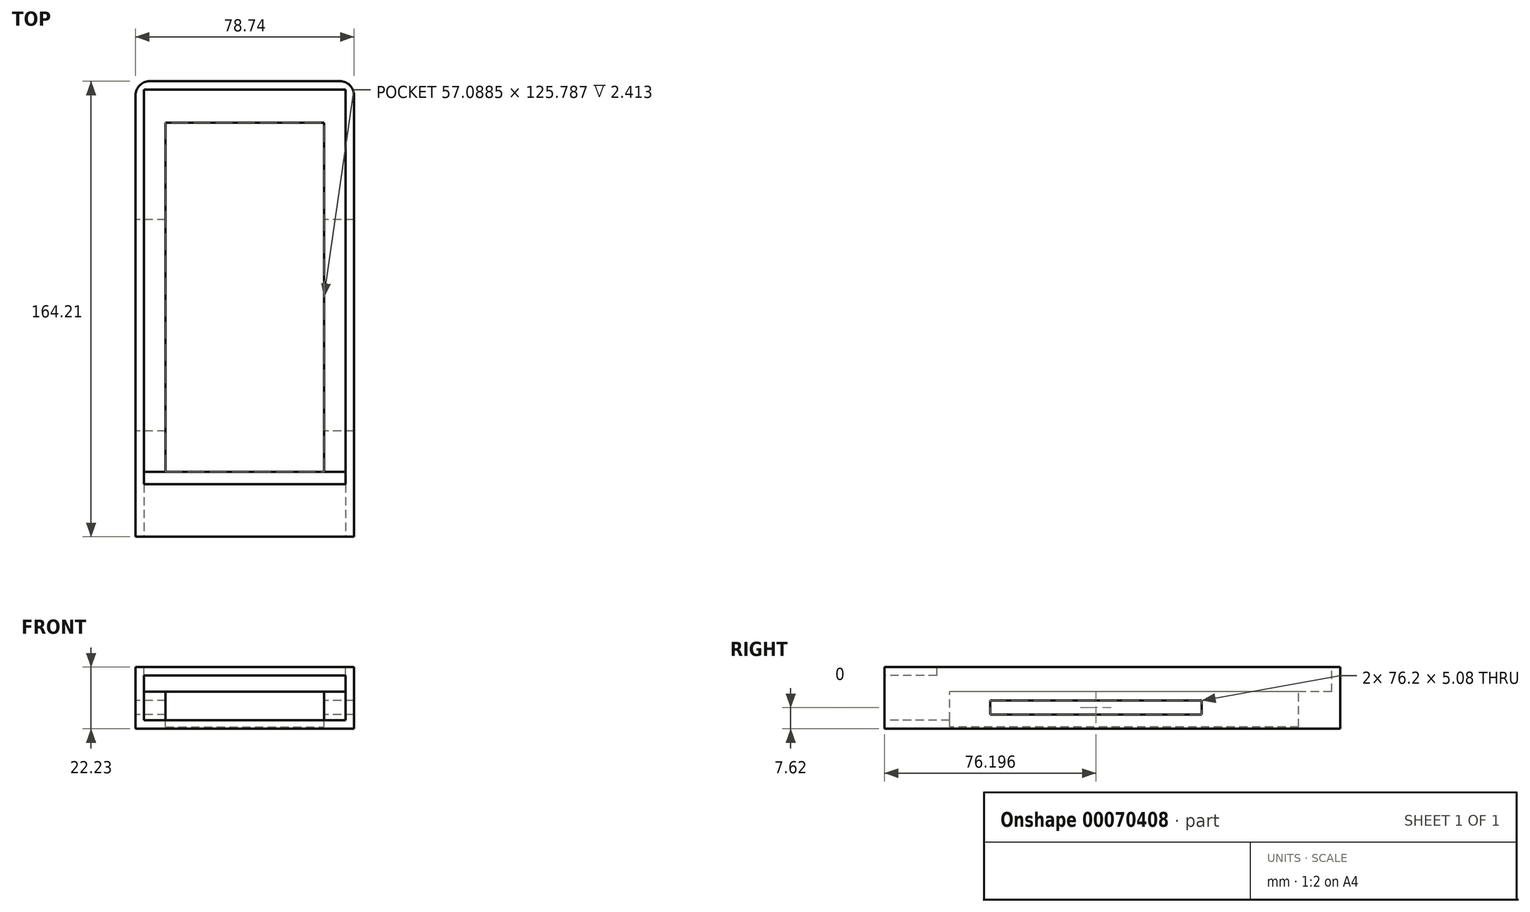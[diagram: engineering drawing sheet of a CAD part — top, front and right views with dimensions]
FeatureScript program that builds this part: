
annotation { "Feature Type Name" : "Feature", "Feature Type Description" : "" }
export const myFeature = defineFeature(function(context is Context, id is Id, definition is map)
    precondition{}
    {
        {
            var Q0;
            Q0=qCreatedBy(makeId("Top.planeOp"),FACE);
            var sketch = newSketch(context, id + "F0", { "sketchPlane" : qUnion([Q0])});
            skLineSegment(sketch, "E0.0", {"start": v(-45.8, 72.92) * mm, "end": v(32.94, 72.92) * mm});
            skLineSegment(sketch, "E0.1", {"start": v(-45.8, 72.92) * mm, "end": v(-45.8, -75.42) * mm});
            skLineSegment(sketch, "E0.2", {"start": v(-45.8, -75.42) * mm, "end": v(32.94, -75.42) * mm});
            skLineSegment(sketch, "E0.3", {"start": v(32.94, 72.92) * mm, "end": v(32.94, -75.42) * mm});
            skLineSegment(sketch, "E1", {"start": v(-45.8, -75.42) * mm, "end": v(-45.8, -91.3) * mm});
            skLineSegment(sketch, "E2", {"start": v(-45.8, -91.3) * mm, "end": v(32.94, -91.3) * mm});
            skLineSegment(sketch, "E3", {"start": v(32.94, -91.3) * mm, "end": v(32.94, -75.42) * mm});
            skSolve(sketch);
        }
        {
            var Q0;
            Q0=makeQuery(id+"F0.imprint","IMPRINT",FACE,{"disambiguationData":[TD([[makeQuery(id+"F0.imprint","IMPRINT",EDGE,{"derivedFrom":sQuery(id+"F0.wireOp",EDGE,"E0.0")}),-1.0]])]});
            extrude(context, id + "F1", {"entities" : qUnion([Q0]), "depth" : 22.22 * mm});
        }
        {
            var Q0;
            Q0=makeQuery(id+"F1.opExtrude","CAP_FACE",FACE,{"disambiguationData":[OSD([sQuery(id+"F0.wireOp",EDGE,"E0.0"),sQuery(id+"F0.wireOp",EDGE,"E0.1"),sQuery(id+"F0.wireOp",EDGE,"E0.2"),sQuery(id+"F0.wireOp",EDGE,"E0.3")])],"isStart":false});
            var sketch = newSketch(context, id + "F2", { "sketchPlane" : qUnion([Q0])});
            skLineSegment(sketch, "E4.bottom", {"start": v(-45.8, 72.92) * mm, "end": v(32.94, 72.92) * mm});
            skLineSegment(sketch, "E4.top", {"start": v(-45.8, -75.42) * mm, "end": v(32.94, -75.42) * mm});
            skLineSegment(sketch, "E4.left", {"start": v(-45.8, 72.92) * mm, "end": v(-45.8, -75.42) * mm});
            skLineSegment(sketch, "E4.right", {"start": v(32.94, 72.92) * mm, "end": v(32.94, -75.42) * mm});
            skLineSegment(sketch, "E5.0", {"start": v(-42.75, 69.87) * mm, "end": v(29.9, 69.87) * mm});
            skLineSegment(sketch, "E5.1", {"start": v(-42.75, 69.87) * mm, "end": v(-42.75, -72.37) * mm});
            skLineSegment(sketch, "E5.2", {"start": v(-42.75, -72.37) * mm, "end": v(29.9, -72.37) * mm});
            skLineSegment(sketch, "E5.3", {"start": v(29.9, 69.87) * mm, "end": v(29.9, -72.37) * mm});
            skSolve(sketch);
        }
        {
            var Q0;
            Q0=makeQuery(id+"F2.imprint","IMPRINT",FACE,{"disambiguationData":[TD([[makeQuery(id+"F2.imprint","IMPRINT",EDGE,{"derivedFrom":sQuery(id+"F2.wireOp",EDGE,"E5.0")}),-1.0]])]});
            extrude(context, id + "F3", {"entities" : qUnion([Q0]), "operationType" : NewBodyOperationType.REMOVE, "oppositeDirection" : true, "depth" : 8.9 * mm});
        }
        {
            var Q0;
            Q0=makeQuery(id+"F3.boolean.opBoolean","COPY",FACE,{"derivedFrom":makeQuery(id+"F3.opExtrude","CAP_FACE",FACE,{"disambiguationData":[OSD([sQuery(id+"F2.wireOp",EDGE,"E5.0"),sQuery(id+"F2.wireOp",EDGE,"E5.1"),sQuery(id+"F2.wireOp",EDGE,"E5.2"),sQuery(id+"F2.wireOp",EDGE,"E5.3")])],"isStart":false})});
            var sketch = newSketch(context, id + "F4", { "sketchPlane" : qUnion([Q0])});
            skLineSegment(sketch, "E6.bottom", {"start": v(-34.97, 57.94) * mm, "end": v(22.12, 57.94) * mm});
            skLineSegment(sketch, "E6.top", {"start": v(-34.97, -67.85) * mm, "end": v(22.12, -67.85) * mm});
            skLineSegment(sketch, "E6.left", {"start": v(-34.97, 57.94) * mm, "end": v(-34.97, -67.85) * mm});
            skLineSegment(sketch, "E6.right", {"start": v(22.12, 57.94) * mm, "end": v(22.12, -67.85) * mm});
            skLineSegment(sketch, "E7", {"start": v(-6.43, 69.87) * mm, "end": v(-6.43, 57.94) * mm});
            skSolve(sketch);
        }
        {
            var Q0;
            Q0=makeQuery(id+"F4.imprint","IMPRINT",FACE,{"disambiguationData":[TD([[makeQuery(id+"F4.imprint","IMPRINT",EDGE,{"derivedFrom":sQuery(id+"F4.wireOp",EDGE,"E6.top")}),1.0]])]});
            extrude(context, id + "F5", {"entities" : qUnion([Q0]), "operationType" : NewBodyOperationType.REMOVE, "oppositeDirection" : true, "depth" : 12.7 * mm});
        }
        {
            var Q0;
            Q0=makeQuery(id+"F0.imprint","IMPRINT",FACE,{"disambiguationData":[TD([[makeQuery(id+"F0.imprint","IMPRINT",EDGE,{"derivedFrom":sQuery(id+"F0.wireOp",EDGE,"E0.2")}),-1.0]])]});
            extrude(context, id + "F6", {"entities" : qUnion([Q0]), "operationType" : NewBodyOperationType.ADD, "depth" : 22.22 * mm});
        }
        {
            var Q0;
            Q0=makeQuery(id+"F6.opExtrude","SWEPT_FACE",FACE,{"disambiguationData":[OSD([sQuery(id+"F0.wireOp",EDGE,"E2")])]});
            var sketch = newSketch(context, id + "F7", { "sketchPlane" : qUnion([Q0])});
            skLineSegment(sketch, "E8.0", {"start": v(-42.75, 19.18) * mm, "end": v(29.9, 19.18) * mm});
            skLineSegment(sketch, "E8.1", {"start": v(-42.75, 19.18) * mm, "end": v(-42.75, 3.05) * mm});
            skLineSegment(sketch, "E8.2", {"start": v(-42.75, 3.05) * mm, "end": v(29.9, 3.05) * mm});
            skLineSegment(sketch, "E8.3", {"start": v(29.9, 19.18) * mm, "end": v(29.9, 3.05) * mm});
            skSolve(sketch);
        }
        {
            var Q0;
            Q0=makeQuery(id+"F7.imprint","IMPRINT",FACE,{"disambiguationData":[TD([[makeQuery(id+"F7.imprint","IMPRINT",EDGE,{"derivedFrom":sQuery(id+"F7.wireOp",EDGE,"E8.0")}),-1.0]])]});
            var Q1;
            Q1=makeQuery(id+"F5.boolean.opBoolean","COPY",FACE,{"derivedFrom":makeQuery(id+"F5.opExtrude","SWEPT_FACE",FACE,{"disambiguationData":[OSD([sQuery(id+"F4.wireOp",EDGE,"E6.top")])]})});
            extrude(context, id + "F8", {"entities" : qUnion([Q0]), "operationType" : NewBodyOperationType.REMOVE, "endBound" : BoundingType.UP_TO_SURFACE, "oppositeDirection" : true, "endBoundEntityFace" : qUnion([Q1]), "depth" : 20.48 * mm});
        }
        {
            var Q0;
            Q0=makeQuery(id+"F6.boolean.opBoolean","MERGE",FACE,{"derivedFrom":[makeQuery(id+"F1.opExtrude","SWEPT_FACE",FACE,{"disambiguationData":[OSD([sQuery(id+"F0.wireOp",EDGE,"E0.1")])]}),makeQuery(id+"F6.opExtrude","SWEPT_FACE",FACE,{"disambiguationData":[OSD([sQuery(id+"F0.wireOp",EDGE,"E1")])]})]});
            var sketch = newSketch(context, id + "F9", { "sketchPlane" : qUnion([Q0])});
            skLineSegment(sketch, "E9.bottom", {"start": v(-23, 10.16) * mm, "end": v(53.2, 10.16) * mm});
            skLineSegment(sketch, "E9.top", {"start": v(-23, 5.08) * mm, "end": v(53.2, 5.08) * mm});
            skLineSegment(sketch, "E9.left", {"start": v(-23, 10.16) * mm, "end": v(-23, 5.08) * mm});
            skLineSegment(sketch, "E9.right", {"start": v(53.2, 10.16) * mm, "end": v(53.2, 5.08) * mm});
            skSolve(sketch);
        }
        {
            var Q0;
            Q0=makeQuery(id+"F9.imprint","IMPRINT",FACE,{"disambiguationData":[TD([[makeQuery(id+"F9.imprint","IMPRINT",EDGE,{"derivedFrom":sQuery(id+"F9.wireOp",EDGE,"E9.bottom")}),-1.0]])]});
            var Q1;
            Q1=makeQuery(id+"F6.boolean.opBoolean","MERGE",FACE,{"derivedFrom":[makeQuery(id+"F1.opExtrude","SWEPT_FACE",FACE,{"disambiguationData":[OSD([sQuery(id+"F0.wireOp",EDGE,"E0.3")])]}),makeQuery(id+"F6.opExtrude","SWEPT_FACE",FACE,{"disambiguationData":[OSD([sQuery(id+"F0.wireOp",EDGE,"E3")])]})]});
            extrude(context, id + "F10", {"entities" : qUnion([Q0]), "operationType" : NewBodyOperationType.REMOVE, "endBound" : BoundingType.UP_TO_SURFACE, "oppositeDirection" : true, "endBoundEntityFace" : qUnion([Q1]), "depth" : 25.4 * mm});
        }
        {
            var Q0;
            Q0=makeQuery(id+"F1.opExtrude","SWEPT_EDGE",EDGE,{"disambiguationData":[OSD([sQuery(id+"F0.wireOp",EDGE,"E0.0"),sQuery(id+"F0.wireOp",EDGE,"E0.1")])]});
            var Q1;
            Q1=makeQuery(id+"F1.opExtrude","SWEPT_EDGE",EDGE,{"disambiguationData":[OSD([sQuery(id+"F0.wireOp",EDGE,"E0.0"),sQuery(id+"F0.wireOp",EDGE,"E0.3")])]});
            fillet(context, id + "F11", {"entities" : qUnion([Q0, Q1]), "radius" : 5.08 * mm, "tangentPropagation" : true, "allowEdgeOverflow" : false});
        }
    });
